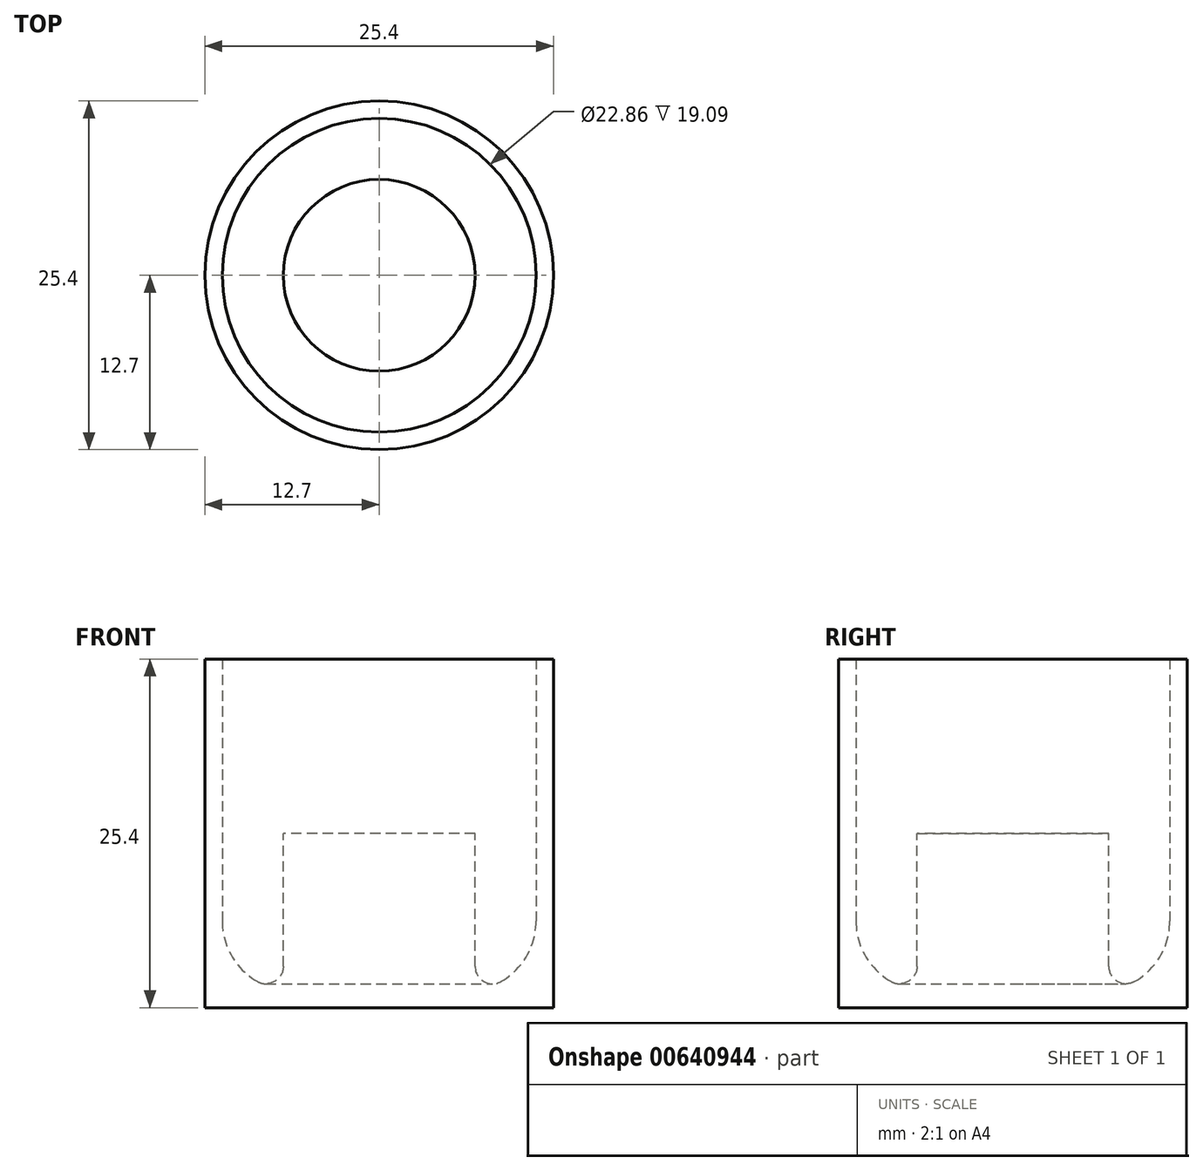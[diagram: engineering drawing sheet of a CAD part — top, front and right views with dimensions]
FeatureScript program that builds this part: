
annotation { "Feature Type Name" : "Feature", "Feature Type Description" : "" }
export const myFeature = defineFeature(function(context is Context, id is Id, definition is map)
    precondition{}
    {
        {
            var Q0;
            Q0=qCreatedBy(makeId("Top.planeOp"),FACE);
            var sketch = newSketch(context, id + "F0", { "sketchPlane" : qUnion([Q0])});
            skCircle(sketch, "E0", {"center": v(0, 0) * mm, "radius": 12.7 * mm});
            skSolve(sketch);
        }
        {
            var Q0;
            Q0=makeQuery(id+"F0.imprint","IMPRINT",FACE,{"disambiguationData":[TD([[makeQuery(id+"F0.imprint","IMPRINT",EDGE,{"derivedFrom":sQuery(id+"F0.wireOp",EDGE,"E0")}),1.0]])]});
            extrude(context, id + "F1", {"entities" : qUnion([Q0]), "depth" : 25.4 * mm, "offsetDistance" : 25.4 * mm});
        }
        {
            var Q0;
            Q0=makeQuery(id+"F1.opExtrude","CAP_FACE",FACE,{"disambiguationData":[OSD([sQuery(id+"F0.wireOp",EDGE,"E0")])],"isStart":false});
            shell(context, id + "F2", {"entities" : qUnion([Q0]), "thickness" : 1.27 * mm});
        }
        {
            var Q0;
            Q0=qCreatedBy(makeId("Top.planeOp"),FACE);
            cPlane(context, id + "F3", {"entities" : qUnion([Q0]), "cplaneType" : CPlaneType.OFFSET, "offset" : 12.7 * mm, "width" : 152.4 * mm, "height" : 152.4 * mm});
        }
        {
            var Q0;
            Q0=qCreatedBy(id+"F3.planeOp",FACE);
            var sketch = newSketch(context, id + "F4", { "sketchPlane" : qUnion([Q0])});
            skCircle(sketch, "E1", {"center": v(0, 0) * mm, "radius": 6.99 * mm});
            skSolve(sketch);
        }
        {
            var Q0;
            Q0=makeQuery(id+"F4.imprint","IMPRINT",FACE,{"disambiguationData":[TD([[makeQuery(id+"F4.imprint","IMPRINT",EDGE,{"derivedFrom":sQuery(id+"F4.wireOp",EDGE,"E1")}),1.0]])]});
            extrude(context, id + "F5", {"entities" : qUnion([Q0]), "operationType" : NewBodyOperationType.ADD, "endBound" : BoundingType.UP_TO_NEXT, "oppositeDirection" : true, "depth" : 25.4 * mm, "offsetDistance" : 25.4 * mm});
        }
        {
            var Q0;
            {var subQ0=sQuery(id+"F0.wireOp",EDGE,"E0");Q0=makeQuery(id+"F2.opShell","OFFSET_EDGE",EDGE,{"disambiguationData":[OSD([subQ0]),TDD([makeQuery(id+"F1.opExtrude","CAP_EDGE",EDGE,{"disambiguationData":[OSD([subQ0])],"isStart":true})])]});}
            fillet(context, id + "F6", {"entities" : qUnion([Q0]), "radius" : 5.08 * mm, "tangentPropagation" : true, "allowEdgeOverflow" : false});
        }
        {
            var Q0;
            {var subQ0=sQuery(id+"F0.wireOp",EDGE,"E0");Q0=makeQuery(id+"F6.opFillet","BLEND_EDGE",EDGE,{"blendedFrom":[makeQuery(id+"F2.opShell","OFFSET_EDGE",EDGE,{"disambiguationData":[OSD([subQ0]),TDD([makeQuery(id+"F1.opExtrude","CAP_EDGE",EDGE,{"disambiguationData":[OSD([subQ0])],"isStart":true})])]}),makeQuery(id+"F5.opExtrude","SWEPT_FACE",FACE,{"disambiguationData":[OSD([sQuery(id+"F4.wireOp",EDGE,"E1")])]})],"blendedInto":[makeQuery(id+"F5.opExtrude","SWEPT_FACE",FACE,{"disambiguationData":[OSD([sQuery(id+"F4.wireOp",EDGE,"E1")])]})]});}
            fillet(context, id + "F7", {"entities" : qUnion([Q0]), "radius" : 1.27 * mm, "tangentPropagation" : true, "allowEdgeOverflow" : false});
        }
    });
